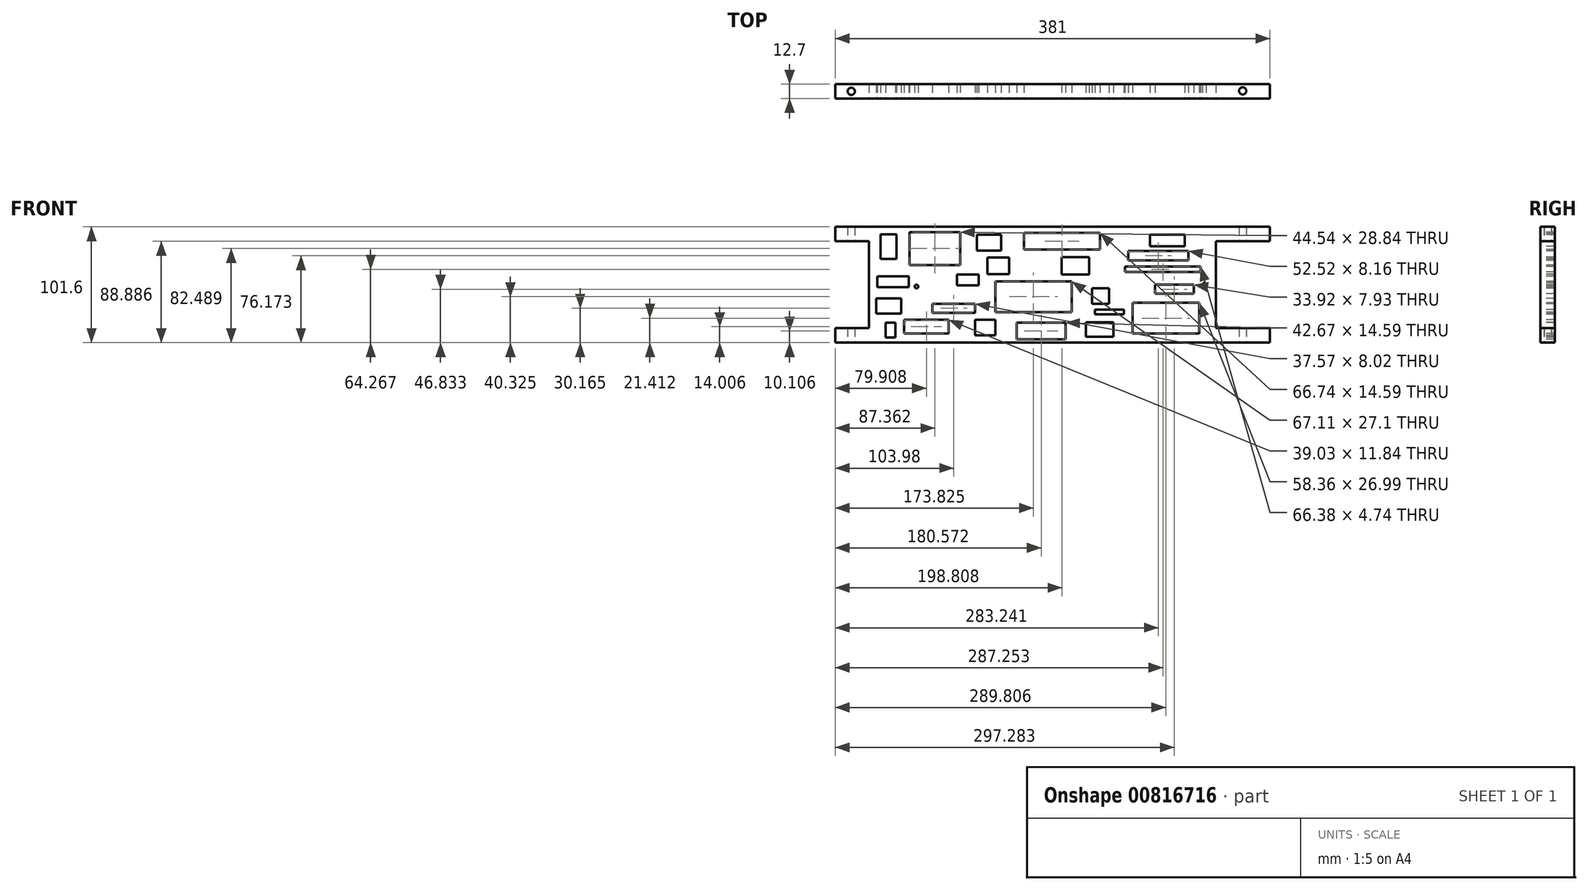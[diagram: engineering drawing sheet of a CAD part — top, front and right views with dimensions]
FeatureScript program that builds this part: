
annotation { "Feature Type Name" : "Feature", "Feature Type Description" : "" }
export const myFeature = defineFeature(function(context is Context, id is Id, definition is map)
    precondition{}
    {
        {
            var Q0;
            Q0=qCreatedBy(makeId("Front.planeOp"),FACE);
            var sketch = newSketch(context, id + "F0", { "sketchPlane" : qUnion([Q0])});
            skLineSegment(sketch, "E0.bottom", {"start": v(-190.5, 50.8) * mm, "end": v(190.5, 50.8) * mm});
            skLineSegment(sketch, "E0.top", {"start": v(-190.5, -50.8) * mm, "end": v(190.5, -50.8) * mm});
            skLineSegment(sketch, "E0.left", {"start": v(-190.5, 50.8) * mm, "end": v(-190.5, -50.8) * mm});
            skLineSegment(sketch, "E0.right", {"start": v(190.5, 50.8) * mm, "end": v(190.5, -50.8) * mm});
            skLineSegment(sketch, "E1", {"start": v(190.5, -50.8) * mm, "end": v(-190.5, 50.8) * mm, "construction": true});
            skSolve(sketch);
        }
        {
            var Q0;
            Q0 = qSketchRegion(id + "F0", true);
            extrude(context, id + "F1", {"entities" : qUnion([Q0]), "depth" : 12.7 * mm, "offsetDistance" : 25.4 * mm});
        }
        {
            var Q0;
            Q0=makeQuery(id+"F1.opExtrude","CAP_FACE",FACE,{"disambiguationData":[OSD([sQuery(id+"F0.wireOp",EDGE,"E0.bottom"),sQuery(id+"F0.wireOp",EDGE,"E0.top"),sQuery(id+"F0.wireOp",EDGE,"E0.left"),sQuery(id+"F0.wireOp",EDGE,"E0.right")])],"isStart":false});
            var sketch = newSketch(context, id + "F2", { "sketchPlane" : qUnion([Q0])});
            skLineSegment(sketch, "E2.bottom", {"start": v(-125.41, 46.1) * mm, "end": v(-80.87, 46.1) * mm});
            skLineSegment(sketch, "E2.top", {"start": v(-125.41, 17.27) * mm, "end": v(-80.87, 17.27) * mm});
            skLineSegment(sketch, "E2.left", {"start": v(-125.41, 46.1) * mm, "end": v(-125.41, 17.27) * mm});
            skLineSegment(sketch, "E2.right", {"start": v(-80.87, 46.1) * mm, "end": v(-80.87, 17.27) * mm});
            skLineSegment(sketch, "E3.bottom", {"start": v(-153.5, 7.45) * mm, "end": v(-126.1, 7.45) * mm});
            skLineSegment(sketch, "E3.top", {"start": v(-153.5, -2.03) * mm, "end": v(-126.1, -2.03) * mm});
            skLineSegment(sketch, "E3.left", {"start": v(-153.5, 7.45) * mm, "end": v(-153.5, -2.03) * mm});
            skLineSegment(sketch, "E3.right", {"start": v(-126.1, 7.45) * mm, "end": v(-126.1, -2.03) * mm});
            skLineSegment(sketch, "E4.bottom", {"start": v(-130.1, -42.71) * mm, "end": v(-91.08, -42.71) * mm});
            skLineSegment(sketch, "E4.top", {"start": v(-130.1, -30.87) * mm, "end": v(-91.08, -30.87) * mm});
            skLineSegment(sketch, "E4.left", {"start": v(-130.1, -30.87) * mm, "end": v(-130.1, -42.71) * mm});
            skLineSegment(sketch, "E4.right", {"start": v(-91.08, -30.87) * mm, "end": v(-91.08, -42.71) * mm});
            skLineSegment(sketch, "E5.bottom", {"start": v(-50.23, -24.02) * mm, "end": v(16.88, -24.02) * mm});
            skLineSegment(sketch, "E5.top", {"start": v(-50.23, 3.07) * mm, "end": v(16.88, 3.07) * mm});
            skLineSegment(sketch, "E5.left", {"start": v(-50.23, -24.02) * mm, "end": v(-50.23, 3.07) * mm});
            skLineSegment(sketch, "E5.right", {"start": v(16.88, -24.02) * mm, "end": v(16.88, 3.07) * mm});
            skLineSegment(sketch, "E6.bottom", {"start": v(-25.06, 30.8) * mm, "end": v(41.68, 30.8) * mm});
            skLineSegment(sketch, "E6.top", {"start": v(-25.06, 45.38) * mm, "end": v(41.68, 45.38) * mm});
            skLineSegment(sketch, "E6.left", {"start": v(-25.06, 30.8) * mm, "end": v(-25.06, 45.38) * mm});
            skLineSegment(sketch, "E6.right", {"start": v(41.68, 30.8) * mm, "end": v(41.68, 45.38) * mm});
            skLineSegment(sketch, "E7.bottom", {"start": v(-83.78, -0.57) * mm, "end": v(-64.82, -0.57) * mm});
            skLineSegment(sketch, "E7.top", {"start": v(-83.78, 8.9) * mm, "end": v(-64.82, 8.9) * mm});
            skLineSegment(sketch, "E7.left", {"start": v(-83.78, -0.57) * mm, "end": v(-83.78, 8.9) * mm});
            skLineSegment(sketch, "E7.right", {"start": v(-64.82, -0.57) * mm, "end": v(-64.82, 8.9) * mm});
            skLineSegment(sketch, "E8.bottom", {"start": v(-105.3, -16.62) * mm, "end": v(-67.74, -16.62) * mm});
            skLineSegment(sketch, "E8.top", {"start": v(-105.3, -24.65) * mm, "end": v(-67.74, -24.65) * mm});
            skLineSegment(sketch, "E8.left", {"start": v(-105.3, -16.62) * mm, "end": v(-105.3, -24.65) * mm});
            skLineSegment(sketch, "E8.right", {"start": v(-67.74, -16.62) * mm, "end": v(-67.74, -24.65) * mm});
            skLineSegment(sketch, "E9.bottom", {"start": v(-31.26, -33.4) * mm, "end": v(11.4, -33.4) * mm});
            skLineSegment(sketch, "E9.top", {"start": v(-31.26, -47.99) * mm, "end": v(11.4, -47.99) * mm});
            skLineSegment(sketch, "E9.left", {"start": v(-31.26, -33.4) * mm, "end": v(-31.26, -47.99) * mm});
            skLineSegment(sketch, "E9.right", {"start": v(11.4, -33.4) * mm, "end": v(11.4, -47.99) * mm});
            skLineSegment(sketch, "E10.bottom", {"start": v(-67.74, -44.34) * mm, "end": v(-50.23, -44.34) * mm});
            skLineSegment(sketch, "E10.top", {"start": v(-67.74, -30.87) * mm, "end": v(-50.23, -30.87) * mm});
            skLineSegment(sketch, "E10.left", {"start": v(-67.74, -30.87) * mm, "end": v(-67.74, -44.34) * mm});
            skLineSegment(sketch, "E10.right", {"start": v(-50.23, -30.87) * mm, "end": v(-50.23, -44.34) * mm});
            skLineSegment(sketch, "E11.bottom", {"start": v(-146.33, -33.4) * mm, "end": v(-137.76, -33.4) * mm});
            skLineSegment(sketch, "E11.top", {"start": v(-146.33, -46.27) * mm, "end": v(-137.76, -46.27) * mm});
            skLineSegment(sketch, "E11.left", {"start": v(-146.33, -33.4) * mm, "end": v(-146.33, -46.27) * mm});
            skLineSegment(sketch, "E11.right", {"start": v(-137.76, -33.4) * mm, "end": v(-137.76, -46.27) * mm});
            skLineSegment(sketch, "E12.bottom", {"start": v(-154.5, -12) * mm, "end": v(-132.66, -12) * mm});
            skLineSegment(sketch, "E12.top", {"start": v(-154.5, -25.38) * mm, "end": v(-132.66, -25.38) * mm});
            skLineSegment(sketch, "E12.left", {"start": v(-154.5, -12) * mm, "end": v(-154.5, -25.38) * mm});
            skLineSegment(sketch, "E12.right", {"start": v(-132.66, -12) * mm, "end": v(-132.66, -25.38) * mm});
            skLineSegment(sketch, "E13.bottom", {"start": v(-150.9, 44.3) * mm, "end": v(-136.82, 44.3) * mm});
            skLineSegment(sketch, "E13.top", {"start": v(-150.9, 22.77) * mm, "end": v(-136.82, 22.77) * mm});
            skLineSegment(sketch, "E13.left", {"start": v(-150.9, 44.3) * mm, "end": v(-150.9, 22.77) * mm});
            skLineSegment(sketch, "E13.right", {"start": v(-136.82, 44.3) * mm, "end": v(-136.82, 22.77) * mm});
            skLineSegment(sketch, "E14.bottom", {"start": v(-57.23, 9.28) * mm, "end": v(-38.2, 9.28) * mm});
            skLineSegment(sketch, "E14.top", {"start": v(-57.23, 23.99) * mm, "end": v(-38.2, 23.99) * mm});
            skLineSegment(sketch, "E14.left", {"start": v(-57.23, 9.28) * mm, "end": v(-57.23, 23.99) * mm});
            skLineSegment(sketch, "E14.right", {"start": v(-38.2, 9.28) * mm, "end": v(-38.2, 23.99) * mm});
            skLineSegment(sketch, "E15.bottom", {"start": v(63.56, 11.1) * mm, "end": v(129.94, 11.1) * mm});
            skLineSegment(sketch, "E15.top", {"start": v(63.56, 15.84) * mm, "end": v(129.94, 15.84) * mm});
            skLineSegment(sketch, "E15.left", {"start": v(63.56, 11.1) * mm, "end": v(63.56, 15.84) * mm});
            skLineSegment(sketch, "E15.right", {"start": v(129.94, 11.1) * mm, "end": v(129.94, 15.84) * mm});
            skLineSegment(sketch, "E16.bottom", {"start": v(70.13, -15.9) * mm, "end": v(128.48, -15.9) * mm});
            skLineSegment(sketch, "E16.top", {"start": v(70.13, -42.88) * mm, "end": v(128.48, -42.88) * mm});
            skLineSegment(sketch, "E16.left", {"start": v(70.13, -15.9) * mm, "end": v(70.13, -42.88) * mm});
            skLineSegment(sketch, "E16.right", {"start": v(128.48, -15.9) * mm, "end": v(128.48, -42.88) * mm});
            skLineSegment(sketch, "E17.bottom", {"start": v(37.3, -26.1) * mm, "end": v(62.47, -26.1) * mm});
            skLineSegment(sketch, "E17.top", {"start": v(37.3, -21.73) * mm, "end": v(62.47, -21.73) * mm});
            skLineSegment(sketch, "E17.left", {"start": v(37.3, -26.1) * mm, "end": v(37.3, -21.73) * mm});
            skLineSegment(sketch, "E17.right", {"start": v(62.47, -26.1) * mm, "end": v(62.47, -21.73) * mm});
            skLineSegment(sketch, "E18.bottom", {"start": v(85.45, 44.05) * mm, "end": v(116.08, 44.05) * mm});
            skLineSegment(sketch, "E18.top", {"start": v(85.45, 33.58) * mm, "end": v(116.08, 33.58) * mm});
            skLineSegment(sketch, "E18.left", {"start": v(85.45, 44.05) * mm, "end": v(85.45, 33.58) * mm});
            skLineSegment(sketch, "E18.right", {"start": v(116.08, 44.05) * mm, "end": v(116.08, 33.58) * mm});
            skLineSegment(sketch, "E19.bottom", {"start": v(66.48, 29.45) * mm, "end": v(119, 29.45) * mm});
            skLineSegment(sketch, "E19.top", {"start": v(66.48, 21.3) * mm, "end": v(119, 21.3) * mm});
            skLineSegment(sketch, "E19.left", {"start": v(66.48, 29.45) * mm, "end": v(66.48, 21.3) * mm});
            skLineSegment(sketch, "E19.right", {"start": v(119, 29.45) * mm, "end": v(119, 21.3) * mm});
            skLineSegment(sketch, "E20.bottom", {"start": v(89.82, 0) * mm, "end": v(123.74, 0) * mm});
            skLineSegment(sketch, "E20.top", {"start": v(89.82, -7.93) * mm, "end": v(123.74, -7.93) * mm});
            skLineSegment(sketch, "E20.left", {"start": v(89.82, -7.93) * mm, "end": v(89.82, 0) * mm});
            skLineSegment(sketch, "E20.right", {"start": v(123.74, -7.93) * mm, "end": v(123.74, 0) * mm});
            skLineSegment(sketch, "E21.bottom", {"start": v(34.75, -3.13) * mm, "end": v(49.7, -3.13) * mm});
            skLineSegment(sketch, "E21.top", {"start": v(34.75, -16.62) * mm, "end": v(49.7, -16.62) * mm});
            skLineSegment(sketch, "E21.left", {"start": v(34.75, -3.13) * mm, "end": v(34.75, -16.62) * mm});
            skLineSegment(sketch, "E21.right", {"start": v(49.7, -3.13) * mm, "end": v(49.7, -16.62) * mm});
            skLineSegment(sketch, "E22.bottom", {"start": v(8.13, 24.18) * mm, "end": v(32.2, 24.18) * mm});
            skLineSegment(sketch, "E22.top", {"start": v(8.13, 9.12) * mm, "end": v(32.2, 9.12) * mm});
            skLineSegment(sketch, "E22.left", {"start": v(8.13, 24.18) * mm, "end": v(8.13, 9.12) * mm});
            skLineSegment(sketch, "E22.right", {"start": v(32.2, 24.18) * mm, "end": v(32.2, 9.12) * mm});
            skLineSegment(sketch, "E23.bottom", {"start": v(-66.28, 43.88) * mm, "end": v(-45.12, 43.88) * mm});
            skLineSegment(sketch, "E23.top", {"start": v(-66.28, 29.79) * mm, "end": v(-45.12, 29.79) * mm});
            skLineSegment(sketch, "E23.left", {"start": v(-66.28, 43.88) * mm, "end": v(-66.28, 29.79) * mm});
            skLineSegment(sketch, "E23.right", {"start": v(-45.12, 43.88) * mm, "end": v(-45.12, 29.79) * mm});
            skLineSegment(sketch, "E24.bottom", {"start": v(143.15, 38.1) * mm, "end": v(190.5, 38.1) * mm});
            skLineSegment(sketch, "E24.top", {"start": v(143.15, -38.1) * mm, "end": v(190.5, -38.1) * mm});
            skLineSegment(sketch, "E24.left", {"start": v(143.15, 38.1) * mm, "end": v(143.15, -38.1) * mm});
            skLineSegment(sketch, "E24.right", {"start": v(190.5, 38.1) * mm, "end": v(190.5, -38.1) * mm});
            skLineSegment(sketch, "E25.top", {"start": v(29.2, -45.65) * mm, "end": v(53.35, -45.65) * mm});
            skLineSegment(sketch, "E25.left", {"start": v(29.2, -32.8) * mm, "end": v(29.2, -45.65) * mm});
            skLineSegment(sketch, "E25.right", {"start": v(53.35, -32.8) * mm, "end": v(53.35, -45.65) * mm});
            skLineSegment(sketch, "E26.bottom", {"start": v(-190.5, 38.1) * mm, "end": v(-161.04, 38.1) * mm});
            skLineSegment(sketch, "E26.top", {"start": v(-190.5, -38.1) * mm, "end": v(-161.04, -38.1) * mm});
            skLineSegment(sketch, "E26.left", {"start": v(-190.5, 38.1) * mm, "end": v(-190.5, -38.1) * mm});
            skLineSegment(sketch, "E26.right", {"start": v(-161.04, 38.1) * mm, "end": v(-161.04, -38.1) * mm});
            skLineSegment(sketch, "E27", {"start": v(29.2, -32.8) * mm, "end": v(53.35, -32.8) * mm});
            skSolve(sketch);
        }
        {
            var Q0;
            Q0 = qSketchRegion(id + "F2", true);
            extrude(context, id + "F3", {"entities" : qUnion([Q0]), "operationType" : NewBodyOperationType.REMOVE, "endBound" : BoundingType.THROUGH_ALL, "oppositeDirection" : true, "depth" : 25.4 * mm, "offsetDistance" : 25.4 * mm});
        }
        {
            var Q0;
            Q0=makeQuery(id+"F1.opExtrude","SWEPT_FACE",FACE,{"disambiguationData":[OSD([sQuery(id+"F0.wireOp",EDGE,"E0.top")])]});
            var sketch = newSketch(context, id + "F4", { "sketchPlane" : qUnion([Q0])});
            skCircle(sketch, "E28", {"center": v(166.72, 5.93) * mm, "radius": 3.18 * mm});
            skCircle(sketch, "E29", {"center": v(-176.4, 6.35) * mm, "radius": 3.18 * mm});
            skPoint(sketch, "E30", {"position": v(-190.5, 6.35) * mm});
            skSolve(sketch);
        }
        {
            var Q0;
            Q0 = qSketchRegion(id + "F4", true);
            extrude(context, id + "F5", {"entities" : qUnion([Q0]), "operationType" : NewBodyOperationType.REMOVE, "endBound" : BoundingType.THROUGH_ALL, "oppositeDirection" : true, "depth" : 25.4 * mm, "offsetDistance" : 25.4 * mm});
        }
        {
            var Q0;
            Q0=makeQuery(id+"F1.opExtrude","CAP_FACE",FACE,{"disambiguationData":[OSD([sQuery(id+"F0.wireOp",EDGE,"E0.bottom"),sQuery(id+"F0.wireOp",EDGE,"E0.top"),sQuery(id+"F0.wireOp",EDGE,"E0.left"),sQuery(id+"F0.wireOp",EDGE,"E0.right")])],"isStart":false});
            var sketch = newSketch(context, id + "F6", { "sketchPlane" : qUnion([Q0])});
            skCircle(sketch, "E31", {"center": v(-119.23, -1.59) * mm, "radius": 1.59 * mm});
            skCircle(sketch, "E32", {"center": v(133.05, 0) * mm, "radius": 1.59 * mm});
            skSolve(sketch);
        }
        {
            var Q0;
            Q0 = qSketchRegion(id + "F6", true);
            extrude(context, id + "F7", {"entities" : qUnion([Q0]), "operationType" : NewBodyOperationType.REMOVE, "endBound" : BoundingType.THROUGH_ALL, "oppositeDirection" : true, "depth" : 25.4 * mm, "offsetDistance" : 25.4 * mm});
        }
    });
